# Revit family: Trap-Primer_Connection Adapter_Zurn_Z1023
name_source: partatom
category: Plumbing Fixtures
units: mm (PartAtom-declared; Revit-internal decimal feet)

## family parameters
Always vertical = Yes
Cut with Voids When Loaded = No
Maintain Annotation Orientation = No
OmniClass Number = 23.45.05.14
OmniClass Title = Plumbing Fixtures - Sanitary Washing Units
Part Type = Normal
Room Calculation Point = No
Round Connector Dimension = Use Radius
Shared = No
Work Plane-Based = No

## types (6) — shared parameters
Assembly Code = D2020100
Body Height = 4.75 "
CW Connection = Yes
CWFU = 1
Connector Radius_B = 0.25 "
DIM_B = 0.5 "
DIM_E = 2.5 "
Default Elevation = 20 "
Description = TRAP PRIMER CONNECTION ADAPTER
HW Connection = No
Main Material = Iron - Zurn - Cast - Painted - Blue
Manufacturer = Zurn Water, LLC
Manufacurer Brand = Zurn
Model = Z1023
Modified Date = 01/27/2026
Product Documentation Link = https://files.zurn.com
Product Page URL = https://www.zurn.com
Product data url = https://www.bimobject.com
URL = www.zurn.com
Vent Connection = No
Waste Connection = No
zero-valued in all types: HWFU, WFU

## per-type parameters (varying)
| type | Approx. Weight (Lbs) | Connector Radius | Pipe Size_A Inside Diameter | Pipe Size_A Nominal Diameter | Pipe Size_A Outer Diameter |
| Z1023_2Inch_No-Hub x No-Hub | 2 " | 1 " | 2.067 " | 2 " | 2.375 " |
| Z1023_3Inch_No-Hub x No-Hub | 4 " | 1.5 " | 3.068 " | 3 " | 3.5 " |
| Z1023_4Inch_No-Hub x No-Hub | 6 " | 2 " | 4.026 " | 4 " | 4.5 " |
| Z1023_2Inch_Threaded x No-Hub | 2 " | 1 " | 2.067 " | 2 " | 2.375 " |
| Z1023_3Inch_Threaded x No-Hub | 4 " | 1.5 " | 3.068 " | 3 " | 3.5 " |
| Z1023_4Inch_Threaded x No-Hub | 6 " | 2 " | 4.026 " | 4 " | 4.5 " |

## geometry (parser evidence)
native form markers: Blend x4, Sweep x2
no freeform markers — native parametric forms only
